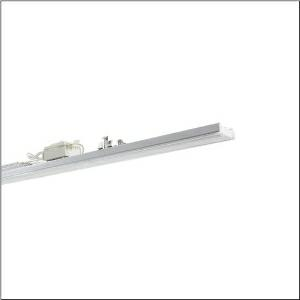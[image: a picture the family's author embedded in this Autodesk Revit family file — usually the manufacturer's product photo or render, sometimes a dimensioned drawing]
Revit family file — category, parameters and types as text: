
# Revit family: licross_r__11_recessed_ho_51te18dv4m1m_3129
name_source: partatom
category: Lighting Fixtures
units: mm (PartAtom-declared; Revit-internal decimal feet)

## family parameters
Cut with Voids When Loaded = No
Host = Face
Light Source = No
Part Type = Normal
Room Calculation Point = No
Round Connector Dimension = Use Diameter
Shared = No

## types (1)
- --- (1 x LED, 26860 lm, 150.5 W, 4000K)
    Apparent Load = 150 VA
    CIE Flux Codes = 78 94 99 100 100
    Color Rendering = 80
    Color Temperature = 4000K
    Default Elevation = 1800 mm
    Description = Licross® 11 Recessed HO, luminaire insert, of sheet steel, galvanised, coil coated, white, length: 2.250mm, width: 66mm, height: 67mm, LED rated luminous flux: 26.870lm, light colour: 840, control gear: DALI 2, with plug, 5-pole, with phase selection, mains connection: 220..240V, AC, 50/60Hz, rated input power: 151W, internal wiring halogen-free, primary light control with lens, of plastic, primary optical cover: cover, of PMMA, light emission: direct distribution, primary light characteristic: symmetric, protection rating (complete): IP54, insulation class (complete): insulation class I (protective earthing), certification: CE, ENEC, VDE, UKCA, protection symbol: D if used in an environment with non-conductive dust loads with corresponding accessories, impact resistance: IK06, permissible ambient temperature for indoor applications: -40..+35°C, corresponds to IFS (International Featured Standards) requirements for safety and quality in the food industry, reducing of maximum allowable ambient temperature of 5°C with ceiling mounting, LABS conformity tested according to VDMA 24364:2018-05, packaging unit: 1 piece
    Height = 58 mm
    Lamp = 1 x LED
    Lamp Light Flux = 26860 lm
    Lamp Power = 150.5 W
    Lamp count = 1
    Length = 2250 mm
    Luminous efficacy = 178 lm/W
    Manufacturer = Siteco
    ModVariant = No
    Model = 51TE18DV4M1M
    Mounting Place = Ceiling
    Mounting Type = Pendant
    Number of Poles = 1
    OnlyDefault = Yes
    Power Factor = 1
    Product Name = Licross® 11 Recessed HO
    Product group = luminaire insert | ceiling pendant
    ProductGroupID = 902
    Protection Class = Protection class I
    Protection Degree = IP 54
    RLX_Detail_Level = 1
    RLX_Emergency_Light_Flux = 0 lm
    RLX_Emergency_Type = 0
    RLX_Emergency_Type_DB = No
    RlxData = <blob elided: 29829 chars, md5=e4780226>
    Socket = socket
    Standby Power = 0 W
    System Light Flux = 26860 lm
    System Power = 150 W
    Type Comments = factory setting: luminous flux: 100 % | dim-lin: 254 | 690 mA
    Type Image = l_1296930.jpg
    URL = http://relux.com
    VarID = @adj_120667
    Voltage = 0 V
    Weight = 0.00 kg
    Width = 66 mm

## geometry (parser evidence)
native form markers: Blend x4, Sweep x11
no freeform markers — native parametric forms only
